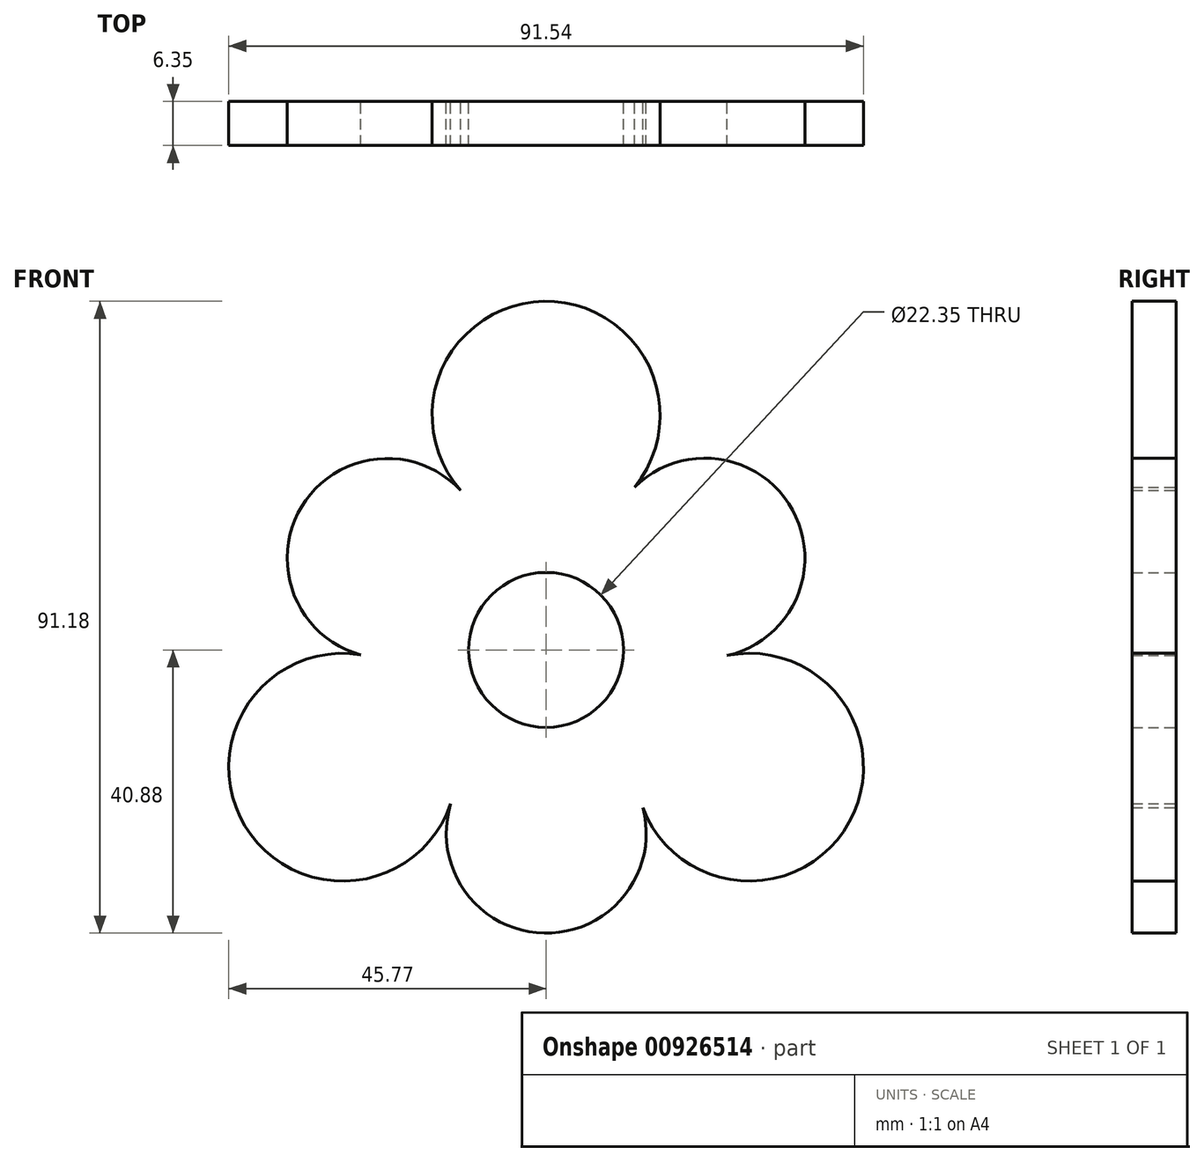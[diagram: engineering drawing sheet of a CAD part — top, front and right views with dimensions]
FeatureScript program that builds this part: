
annotation { "Feature Type Name" : "Feature", "Feature Type Description" : "" }
export const myFeature = defineFeature(function(context is Context, id is Id, definition is map)
    precondition{}
    {
        {
            var Q0;
            Q0=qCreatedBy(makeId("Front.planeOp"),FACE);
            var sketch = newSketch(context, id + "F0", { "sketchPlane" : qUnion([Q0])});
            skCircle(sketch, "E0", {"center": v(0, 0) * mm, "radius": 11.18 * mm});
            skCircle(sketch, "E1", {"center": v(0, 33.87) * mm, "radius": 16.44 * mm});
            skCircle(sketch, "E2.1.0", {"center": v(-29.33, -16.93) * mm, "radius": 16.44 * mm});
            skCircle(sketch, "E2.2.0", {"center": v(29.33, -16.93) * mm, "radius": 16.44 * mm});
            skCircle(sketch, "E3", {"center": v(-22.92, 13.2) * mm, "radius": 14.42 * mm});
            skPoint(sketch, "E3.first.point", {"position": v(-25.11, -1.04) * mm});
            skPoint(sketch, "E3.second.point", {"position": v(-12.35, 23.02) * mm});
            skPoint(sketch, "E3.third.point", {"position": v(-35.84, 19.62) * mm});
            skCircle(sketch, "E4.1.0", {"center": v(0.02, -26.46) * mm, "radius": 14.42 * mm});
            skCircle(sketch, "E4.2.0", {"center": v(22.9, 13.25) * mm, "radius": 14.42 * mm});
            skSolve(sketch);
        }
        {
            var Q0;
            Q0 = qSketchRegion(id + "F0", true);
            var Q1;
            Q1=makeQuery(id+"F0.imprint","IMPRINT",FACE,{"disambiguationData":[TD([[makeQuery(id+"F0.imprint","IMPRINT",EDGE,{"derivedFrom":sQuery(id+"F0.wireOp",EDGE,"E0")}),-1.0]])]});
            extrude(context, id + "F1", {"entities" : qUnion([Q0, Q1]), "depth" : 6.35 * mm, "offsetDistance" : 25.4 * mm});
        }
    });
